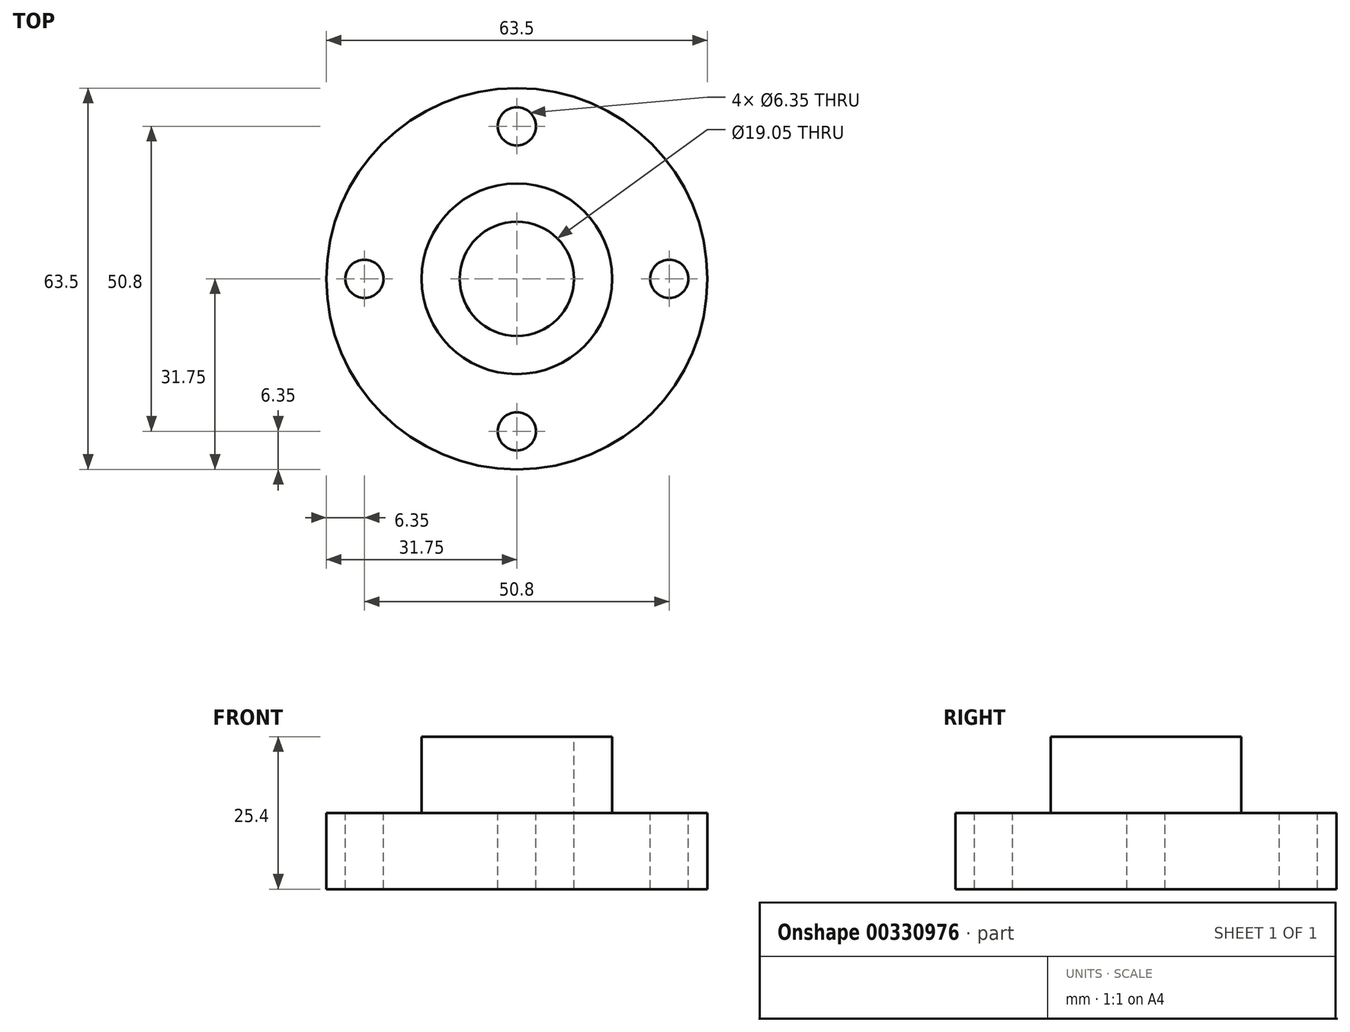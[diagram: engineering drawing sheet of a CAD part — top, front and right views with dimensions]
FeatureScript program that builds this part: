
annotation { "Feature Type Name" : "Feature", "Feature Type Description" : "" }
export const myFeature = defineFeature(function(context is Context, id is Id, definition is map)
    precondition{}
    {
        {
            var Q0;
            Q0=qCreatedBy(makeId("Top.planeOp"),FACE);
            var sketch = newSketch(context, id + "F0", { "sketchPlane" : qUnion([Q0])});
            skCircle(sketch, "E0", {"center": v(0, 0) * mm, "radius": 31.75 * mm});
            skSolve(sketch);
        }
        {
            var Q0;
            Q0 = qSketchRegion(id + "F0", true);
            extrude(context, id + "F1", {"entities" : qUnion([Q0]), "depth" : 12.7 * mm});
        }
        {
            var Q0;
            Q0=makeQuery(id+"F1.opExtrude","CAP_FACE",FACE,{"disambiguationData":[OSD([sQuery(id+"F0.wireOp",EDGE,"E0")])],"isStart":false});
            var sketch = newSketch(context, id + "F2", { "sketchPlane" : qUnion([Q0])});
            skCircle(sketch, "E1", {"center": v(0, 0) * mm, "radius": 25.4 * mm, "construction": true});
            skCircle(sketch, "E2", {"center": v(25.4, 0) * mm, "radius": 3.18 * mm});
            skCircle(sketch, "E3", {"center": v(-25.4, 0) * mm, "radius": 3.18 * mm});
            skCircle(sketch, "E4", {"center": v(0, 25.4) * mm, "radius": 3.18 * mm});
            skCircle(sketch, "E5", {"center": v(0, -25.4) * mm, "radius": 3.18 * mm});
            skSolve(sketch);
        }
        {
            var Q0;
            Q0 = qSketchRegion(id + "F2", true);
            extrude(context, id + "F3", {"entities" : qUnion([Q0]), "operationType" : NewBodyOperationType.REMOVE, "endBound" : BoundingType.THROUGH_ALL, "oppositeDirection" : true, "depth" : 25.4 * mm});
        }
        {
            var Q0;
            Q0=makeQuery(id+"F1.opExtrude","CAP_FACE",FACE,{"disambiguationData":[OSD([sQuery(id+"F0.wireOp",EDGE,"E0")])],"isStart":false});
            var sketch = newSketch(context, id + "F4", { "sketchPlane" : qUnion([Q0])});
            skCircle(sketch, "E6", {"center": v(0, 0) * mm, "radius": 15.88 * mm});
            skSolve(sketch);
        }
        {
            var Q0;
            Q0 = qSketchRegion(id + "F4", true);
            extrude(context, id + "F5", {"entities" : qUnion([Q0]), "operationType" : NewBodyOperationType.ADD, "depth" : 12.7 * mm});
        }
        {
            var Q0;
            Q0=makeQuery(id+"F5.opExtrude","CAP_FACE",FACE,{"disambiguationData":[OSD([sQuery(id+"F4.wireOp",EDGE,"E6")])],"isStart":false});
            var sketch = newSketch(context, id + "F6", { "sketchPlane" : qUnion([Q0])});
            skCircle(sketch, "E7", {"center": v(0, 0) * mm, "radius": 9.53 * mm});
            skSolve(sketch);
        }
        {
            var Q0;
            Q0 = qSketchRegion(id + "F6", true);
            extrude(context, id + "F7", {"entities" : qUnion([Q0]), "operationType" : NewBodyOperationType.REMOVE, "endBound" : BoundingType.THROUGH_ALL, "oppositeDirection" : true, "depth" : 25.4 * mm});
        }
    });
